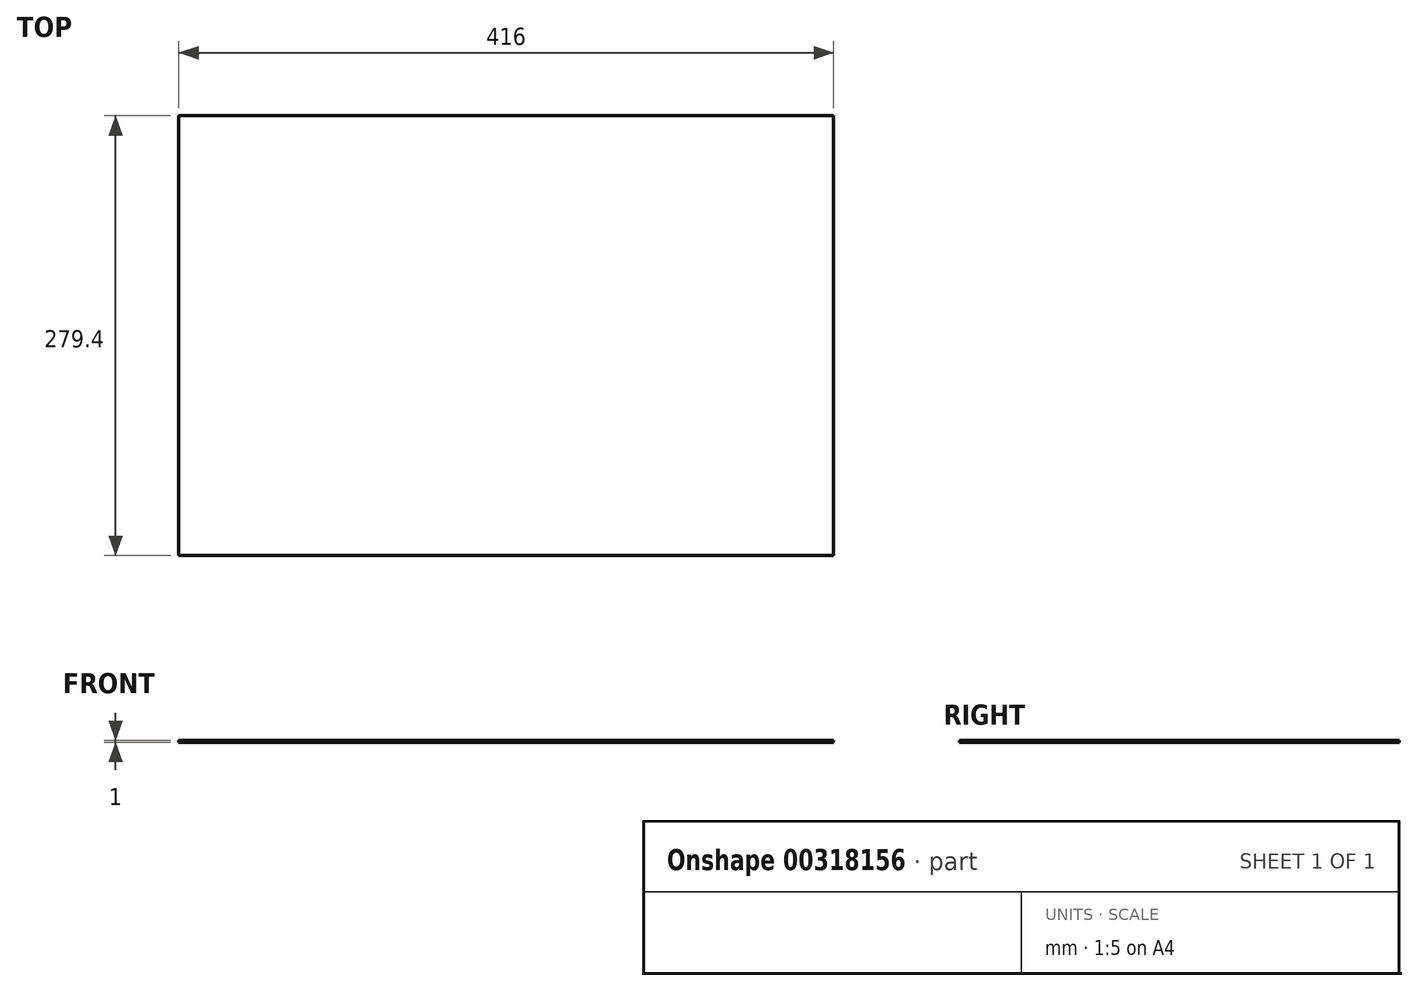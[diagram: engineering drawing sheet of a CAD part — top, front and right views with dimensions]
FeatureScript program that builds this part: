
annotation { "Feature Type Name" : "Feature", "Feature Type Description" : "" }
export const myFeature = defineFeature(function(context is Context, id is Id, definition is map)
    precondition{}
    {
        {
            var Q0;
            Q0=qCreatedBy(makeId("Top.planeOp"),FACE);
            var sketch = newSketch(context, id + "F0", { "sketchPlane" : qUnion([Q0])});
            skLineSegment(sketch, "E0", {"start": v(-212.47, 236.57) * mm, "end": v(-212.47, -42.83) * mm});
            skLineSegment(sketch, "E1", {"start": v(-212.47, -42.83) * mm, "end": v(203.53, -42.83) * mm});
            skLineSegment(sketch, "E2", {"start": v(203.53, -42.83) * mm, "end": v(203.53, 236.57) * mm});
            skLineSegment(sketch, "E3", {"start": v(203.53, 236.57) * mm, "end": v(-212.47, 236.57) * mm});
            skSolve(sketch);
        }
        {
            var Q0;
            Q0=makeQuery(id+"F0.imprint","IMPRINT",FACE,{"disambiguationData":[TD([[makeQuery(id+"F0.imprint","IMPRINT",EDGE,{"derivedFrom":sQuery(id+"F0.wireOp",EDGE,"E0")}),1.0]])]});
            extrude(context, id + "F1", {"entities" : qUnion([Q0]), "depth" : 1 * mm});
        }
    });
